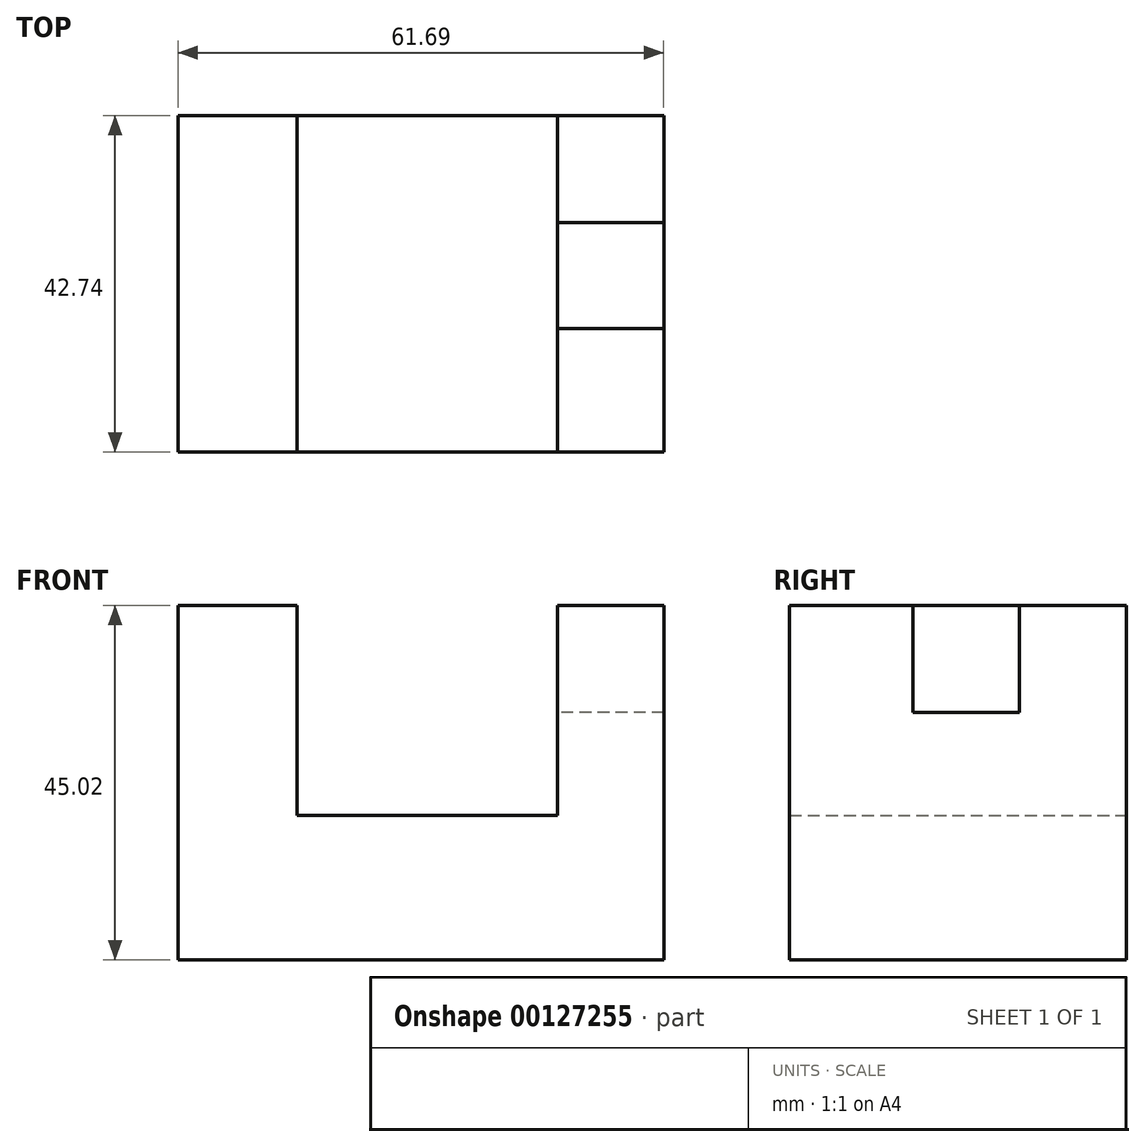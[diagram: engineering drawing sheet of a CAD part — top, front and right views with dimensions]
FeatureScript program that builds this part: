
annotation { "Feature Type Name" : "Feature", "Feature Type Description" : "" }
export const myFeature = defineFeature(function(context is Context, id is Id, definition is map)
    precondition{}
    {
        {
            var Q0;
            Q0=qCreatedBy(makeId("Front.planeOp"),FACE);
            var sketch = newSketch(context, id + "F0", { "sketchPlane" : qUnion([Q0])});
            skLineSegment(sketch, "E0.bottom", {"start": v(0, 0) * mm, "end": v(61.7, 0) * mm});
            skLineSegment(sketch, "E0.top", {"start": v(0, 45.02) * mm, "end": v(15.14, 45.02) * mm});
            skLineSegment(sketch, "E0.left", {"start": v(0, 0) * mm, "end": v(0, 45.02) * mm});
            skLineSegment(sketch, "E0.right", {"start": v(61.7, 0) * mm, "end": v(61.7, 45.02) * mm});
            skLineSegment(sketch, "E1.top", {"start": v(15.14, 18.35) * mm, "end": v(48.19, 18.35) * mm});
            skLineSegment(sketch, "E1.left", {"start": v(15.14, 45.02) * mm, "end": v(15.14, 18.35) * mm});
            skLineSegment(sketch, "E1.right", {"start": v(48.19, 45.02) * mm, "end": v(48.19, 18.35) * mm});
            skLineSegment(sketch, "E2.trimOffspring", {"start": v(48.19, 45.02) * mm, "end": v(61.7, 45.02) * mm});
            skSolve(sketch);
        }
        {
            var Q0;
            Q0=makeQuery(id+"F0.imprint","IMPRINT",FACE,{"disambiguationData":[TD([[makeQuery(id+"F0.imprint","IMPRINT",EDGE,{"derivedFrom":sQuery(id+"F0.wireOp",EDGE,"E0.bottom")}),1.0]])]});
            extrude(context, id + "F1", {"entities" : qUnion([Q0]), "depth" : 42.74 * mm});
        }
        {
            var Q0;
            Q0=makeQuery(id+"F1.opExtrude","SWEPT_FACE",FACE,{"disambiguationData":[OSD([sQuery(id+"F0.wireOp",EDGE,"E2.trimOffspring")])]});
            var sketch = newSketch(context, id + "F2", { "sketchPlane" : qUnion([Q0])});
            skLineSegment(sketch, "E3.bottom", {"start": v(61.7, -27.08) * mm, "end": v(48.19, -27.08) * mm});
            skLineSegment(sketch, "E3.top", {"start": v(61.7, -13.58) * mm, "end": v(48.19, -13.58) * mm});
            skLineSegment(sketch, "E3.left", {"start": v(61.7, -27.08) * mm, "end": v(61.7, -13.58) * mm});
            skLineSegment(sketch, "E3.right", {"start": v(48.19, -27.08) * mm, "end": v(48.19, -13.58) * mm});
            skSolve(sketch);
        }
        {
            var Q0;
            Q0=makeQuery(id+"F2.imprint","IMPRINT",FACE,{"disambiguationData":[TD([[makeQuery(id+"F2.imprint","IMPRINT",EDGE,{"derivedFrom":sQuery(id+"F2.wireOp",EDGE,"E3.bottom")}),-1.0]])]});
            extrude(context, id + "F3", {"entities" : qUnion([Q0]), "operationType" : NewBodyOperationType.REMOVE, "oppositeDirection" : true, "depth" : 13.58 * mm});
        }
    });
